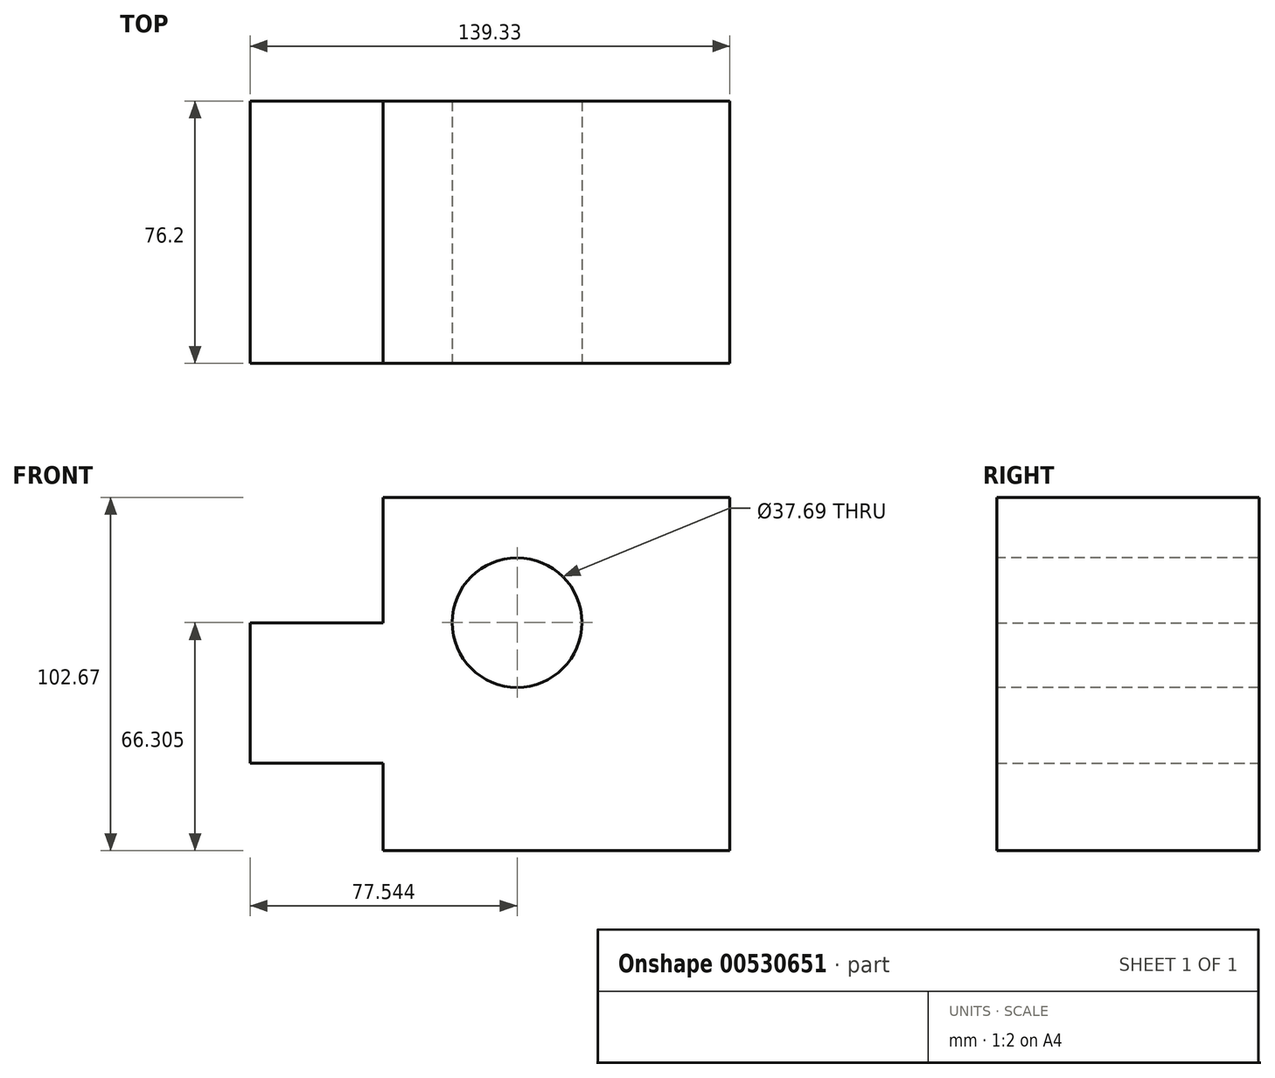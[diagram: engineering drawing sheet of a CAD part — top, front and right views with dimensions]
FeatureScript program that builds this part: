
annotation { "Feature Type Name" : "Feature", "Feature Type Description" : "" }
export const myFeature = defineFeature(function(context is Context, id is Id, definition is map)
    precondition{}
    {
        {
            var Q0;
            Q0=qCreatedBy(makeId("Front.planeOp"),FACE);
            var sketch = newSketch(context, id + "F0", { "sketchPlane" : qUnion([Q0])});
            skLineSegment(sketch, "E0.bottom", {"start": v(-96.17, 17.34) * mm, "end": v(-57.54, 17.34) * mm});
            skLineSegment(sketch, "E0.top", {"start": v(-96.17, -23.45) * mm, "end": v(-57.54, -23.45) * mm});
            skLineSegment(sketch, "E0.left", {"start": v(-96.17, 17.34) * mm, "end": v(-96.17, -23.45) * mm});
            skLineSegment(sketch, "E1.bottom", {"start": v(-57.54, 53.8) * mm, "end": v(43.16, 53.8) * mm});
            skLineSegment(sketch, "E1.top", {"start": v(-57.54, -48.87) * mm, "end": v(43.16, -48.87) * mm});
            skLineSegment(sketch, "E1.left", {"start": v(-57.54, 53.8) * mm, "end": v(-57.54, 17.34) * mm});
            skLineSegment(sketch, "E1.right", {"start": v(43.16, 53.8) * mm, "end": v(43.16, -48.87) * mm});
            skLineSegment(sketch, "E2.trimOffspring", {"start": v(-57.54, -23.45) * mm, "end": v(-57.54, -48.87) * mm});
            skSolve(sketch);
        }
        {
            var Q0;
            Q0=makeQuery(id+"F0.imprint","IMPRINT",FACE,{"disambiguationData":[TD([[makeQuery(id+"F0.imprint","IMPRINT",EDGE,{"derivedFrom":sQuery(id+"F0.wireOp",EDGE,"E0.bottom")}),-1.0]])]});
            extrude(context, id + "F1", {"entities" : qUnion([Q0]), "depth" : 76.2 * mm, "offsetDistance" : 25.4 * mm});
        }
        {
            var Q0;
            Q0=makeQuery(id+"F1.opExtrude","CAP_FACE",FACE,{"disambiguationData":[OSD([sQuery(id+"F0.wireOp",EDGE,"E0.bottom"),sQuery(id+"F0.wireOp",EDGE,"E0.top"),sQuery(id+"F0.wireOp",EDGE,"E0.left"),sQuery(id+"F0.wireOp",EDGE,"E1.bottom"),sQuery(id+"F0.wireOp",EDGE,"E1.top"),sQuery(id+"F0.wireOp",EDGE,"E1.left"),sQuery(id+"F0.wireOp",EDGE,"E1.right"),sQuery(id+"F0.wireOp",EDGE,"E2.trimOffspring")])],"isStart":false});
            var sketch = newSketch(context, id + "F2", { "sketchPlane" : qUnion([Q0])});
            skCircle(sketch, "E3", {"center": v(-18.63, 17.43) * mm, "radius": 18.84 * mm});
            skSolve(sketch);
        }
        {
            var Q0;
            Q0=makeQuery(id+"F2.imprint","IMPRINT",FACE,{"disambiguationData":[TD([[makeQuery(id+"F2.imprint","IMPRINT",EDGE,{"derivedFrom":sQuery(id+"F2.wireOp",EDGE,"E3")}),1.0]])]});
            extrude(context, id + "F3", {"entities" : qUnion([Q0]), "operationType" : NewBodyOperationType.REMOVE, "oppositeDirection" : true, "depth" : 76.2 * mm, "offsetDistance" : 25.4 * mm});
        }
    });
